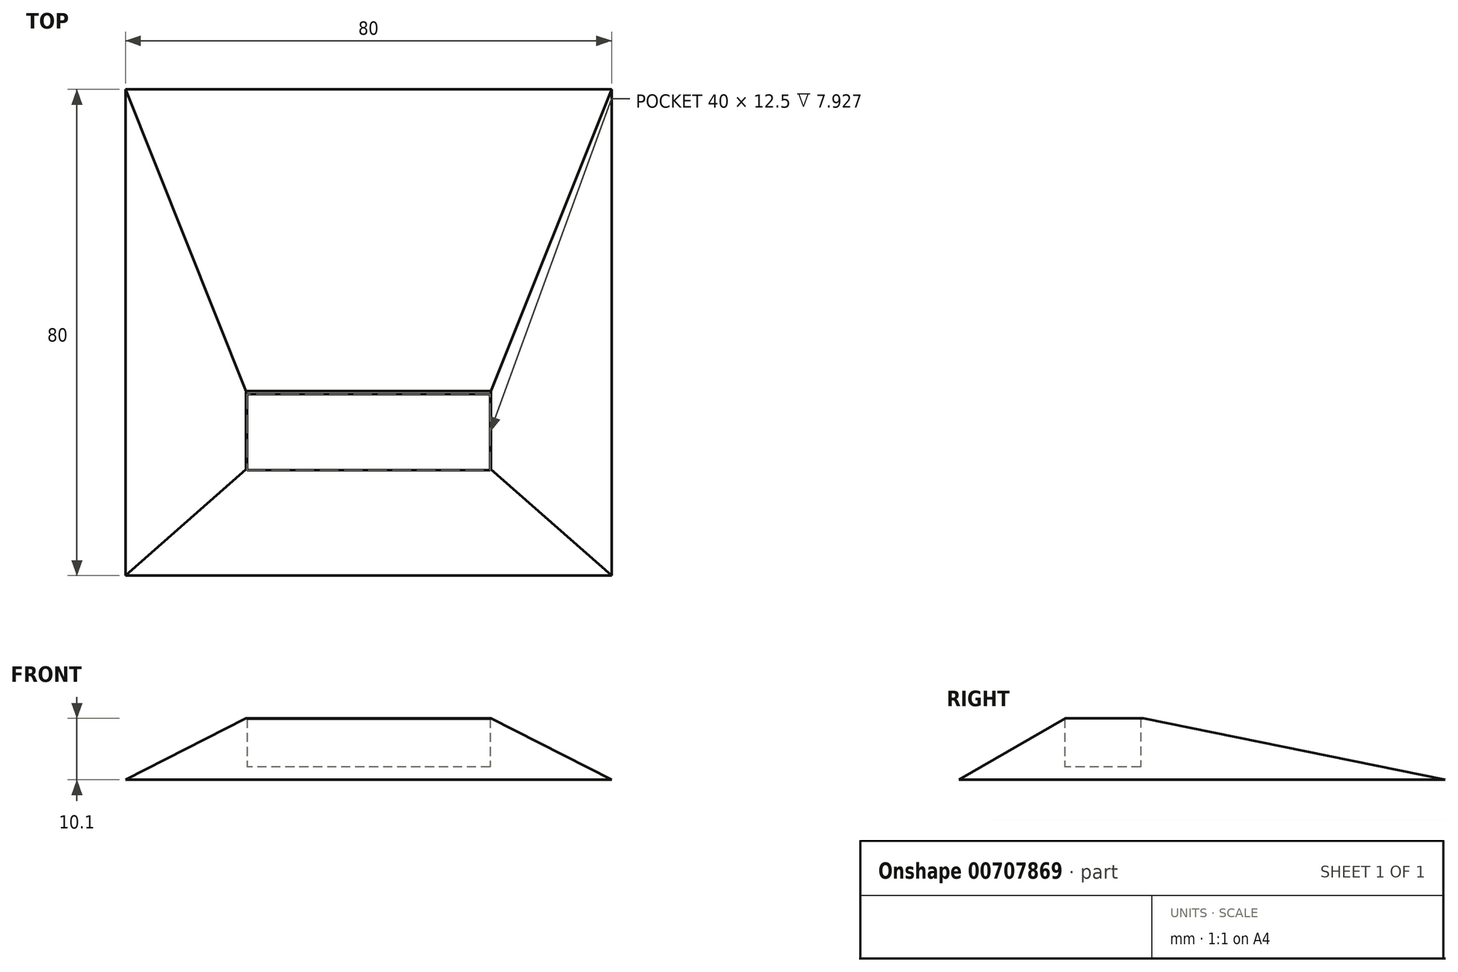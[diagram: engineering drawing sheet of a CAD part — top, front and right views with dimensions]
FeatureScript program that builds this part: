
annotation { "Feature Type Name" : "Feature", "Feature Type Description" : "" }
export const myFeature = defineFeature(function(context is Context, id is Id, definition is map)
    precondition{}
    {
        {
            var Q0;
            Q0=qCreatedBy(makeId("Top.planeOp"),FACE);
            var sketch = newSketch(context, id + "F0", { "sketchPlane" : qUnion([Q0])});
            skLineSegment(sketch, "E0.bottom", {"start": v(40, -40) * mm, "end": v(-40, -40) * mm});
            skLineSegment(sketch, "E0.top", {"start": v(40, 40) * mm, "end": v(-40, 40) * mm});
            skLineSegment(sketch, "E0.left", {"start": v(40, -40) * mm, "end": v(40, 40) * mm});
            skLineSegment(sketch, "E0.right", {"start": v(-40, -40) * mm, "end": v(-40, 40) * mm});
            skPoint(sketch, "E0.middle", {"position": v(0, 0) * mm});
            skLineSegment(sketch, "E1.bottom", {"start": v(20, -10.13) * mm, "end": v(-20, -10.13) * mm});
            skLineSegment(sketch, "E1.top", {"start": v(20, -22.63) * mm, "end": v(-20, -22.63) * mm});
            skLineSegment(sketch, "E1.left", {"start": v(20, -10.13) * mm, "end": v(20, -22.63) * mm});
            skLineSegment(sketch, "E1.right", {"start": v(-20, -10.13) * mm, "end": v(-20, -22.63) * mm});
            skPoint(sketch, "E1.middle", {"position": v(0, -16.38) * mm});
            skSolve(sketch);
        }
        {
            var Q0;
            Q0=makeQuery(id+"F0.imprint","IMPRINT",FACE,{"disambiguationData":[TD([[makeQuery(id+"F0.imprint","IMPRINT",EDGE,{"derivedFrom":sQuery(id+"F0.wireOp",EDGE,"E0.bottom")}),-1.0]])]});
            extrude(context, id + "F1", {"entities" : qUnion([Q0]), "depth" : 10.1 * mm, "offsetDistance" : 25 * mm});
        }
        {
            var Q0;
            Q0=makeQuery(id+"F1.opExtrude","CAP_EDGE",EDGE,{"disambiguationData":[OSD([sQuery(id+"F0.wireOp",EDGE,"E0.bottom")])],"isStart":false});
            chamfer(context, id + "F2", {"entities" : qUnion([Q0]), "chamferType" : ChamferType.OFFSET_ANGLE, "width" : 10.1 * mm, "oppositeDirection" : false, "angle" : 60 * degree});
        }
        {
            var Q0;
            Q0=makeQuery(id+"F1.opExtrude","CAP_EDGE",EDGE,{"disambiguationData":[OSD([sQuery(id+"F0.wireOp",EDGE,"E0.right")])],"isStart":false});
            var Q1;
            Q1=makeQuery(id+"F1.opExtrude","CAP_EDGE",EDGE,{"disambiguationData":[OSD([sQuery(id+"F0.wireOp",EDGE,"E0.left")])],"isStart":false});
            chamfer(context, id + "F3", {"entities" : qUnion([Q0, Q1]), "chamferType" : ChamferType.OFFSET_ANGLE, "width" : 10.1 * mm, "oppositeDirection" : false, "angle" : 63 * degree, "tangentPropagation" : true});
        }
        {
            var Q0;
            Q0=makeQuery(id+"F1.opExtrude","CAP_EDGE",EDGE,{"disambiguationData":[OSD([sQuery(id+"F0.wireOp",EDGE,"E0.top")])],"isStart":false});
            chamfer(context, id + "F4", {"entities" : qUnion([Q0]), "chamferType" : ChamferType.OFFSET_ANGLE, "width" : 10.1 * mm, "oppositeDirection" : true, "angle" : 78.5 * degree, "tangentPropagation" : true});
        }
        {
            var Q0;
            Q0=makeQuery(id+"F0.imprint","IMPRINT",FACE,{"disambiguationData":[TD([[makeQuery(id+"F0.imprint","IMPRINT",EDGE,{"derivedFrom":sQuery(id+"F0.wireOp",EDGE,"E1.bottom")}),1.0]])]});
            extrude(context, id + "F5", {"entities" : qUnion([Q0]), "operationType" : NewBodyOperationType.ADD, "depth" : 2.1 * mm, "offsetDistance" : 25 * mm});
        }
    });
